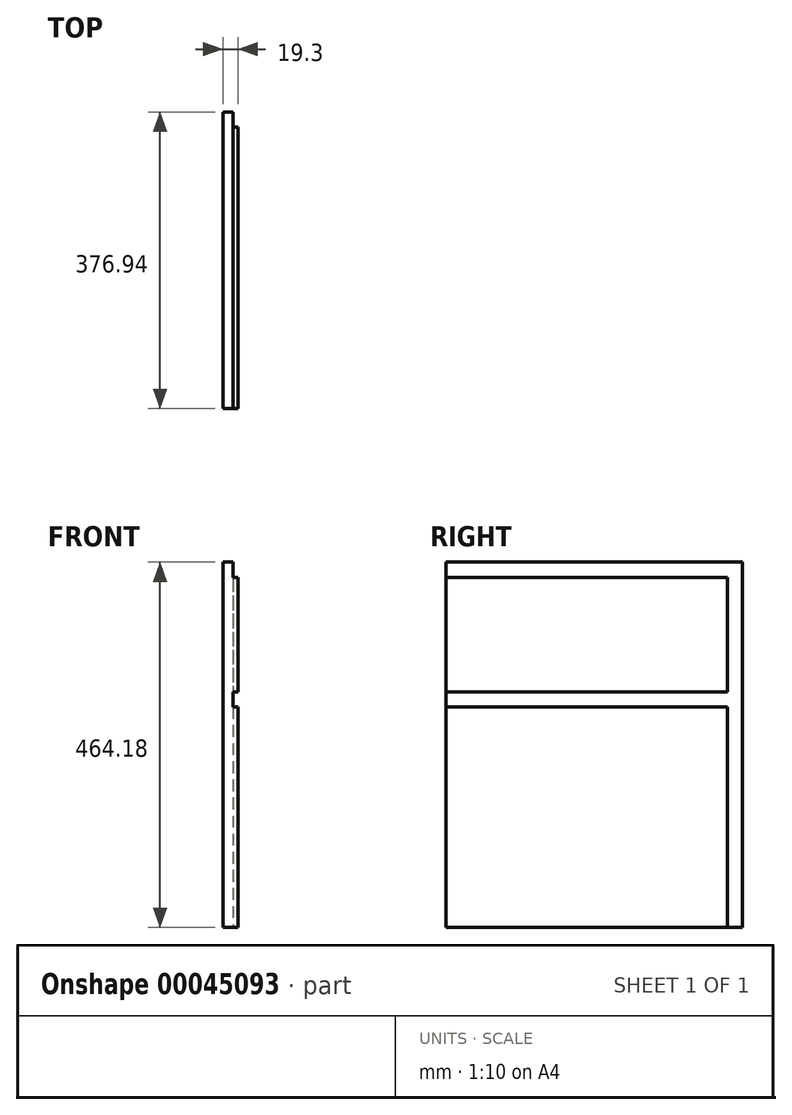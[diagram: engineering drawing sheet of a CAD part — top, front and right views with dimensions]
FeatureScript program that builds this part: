
annotation { "Feature Type Name" : "Feature", "Feature Type Description" : "" }
export const myFeature = defineFeature(function(context is Context, id is Id, definition is map)
    precondition{}
    {
        {
            var Q0;
            Q0=qCreatedBy(makeId("Right.planeOp"),FACE);
            var sketch = newSketch(context, id + "F0", { "sketchPlane" : qUnion([Q0])});
            skLineSegment(sketch, "E0.rect.bottom", {"start": v(-188.47, 232.1) * mm, "end": v(188.47, 232.1) * mm});
            skLineSegment(sketch, "E0.rect.top", {"start": v(-188.47, -232.1) * mm, "end": v(188.47, -232.1) * mm});
            skLineSegment(sketch, "E0.rect.left", {"start": v(-188.47, 232.1) * mm, "end": v(-188.47, -232.1) * mm});
            skLineSegment(sketch, "E0.rect.right", {"start": v(188.47, 232.1) * mm, "end": v(188.47, -232.1) * mm});
            skPoint(sketch, "E0.rect.middle", {"position": v(0, 0) * mm});
            skSolve(sketch);
        }
        {
            var Q0;
            Q0 = qSketchRegion(id + "F0", true);
            extrude(context, id + "F1", {"entities" : qUnion([Q0]), "depth" : 19.3 * mm});
        }
        {
            var Q0;
            Q0=makeQuery(id+"F1.opExtrude","CAP_FACE",FACE,{"disambiguationData":[OSD([sQuery(id+"F0.wireOp",EDGE,"E0.rect.bottom"),sQuery(id+"F0.wireOp",EDGE,"E0.rect.top"),sQuery(id+"F0.wireOp",EDGE,"E0.rect.left"),sQuery(id+"F0.wireOp",EDGE,"E0.rect.right")])],"isStart":false});
            var sketch = newSketch(context, id + "F2", { "sketchPlane" : qUnion([Q0])});
            skLineSegment(sketch, "E1.bottom", {"start": v(-188.47, 67.37) * mm, "end": v(188.47, 67.37) * mm});
            skLineSegment(sketch, "E1.top", {"start": v(-188.47, 48.07) * mm, "end": v(188.47, 48.07) * mm});
            skLineSegment(sketch, "E1.left", {"start": v(-188.47, 67.37) * mm, "end": v(-188.47, 48.07) * mm});
            skLineSegment(sketch, "E1.right", {"start": v(188.47, 67.37) * mm, "end": v(188.47, 48.07) * mm});
            skLineSegment(sketch, "E2.bottom", {"start": v(188.47, 232.1) * mm, "end": v(169.16, 232.1) * mm});
            skLineSegment(sketch, "E2.top", {"start": v(188.47, -232.1) * mm, "end": v(169.16, -232.1) * mm});
            skLineSegment(sketch, "E2.left", {"start": v(188.47, 232.1) * mm, "end": v(188.47, -232.1) * mm});
            skLineSegment(sketch, "E2.right", {"start": v(169.16, 232.1) * mm, "end": v(169.16, -232.1) * mm});
            skLineSegment(sketch, "E3.bottom", {"start": v(-188.47, 232.1) * mm, "end": v(188.47, 232.1) * mm});
            skLineSegment(sketch, "E3.top", {"start": v(-188.47, 212.79) * mm, "end": v(188.47, 212.79) * mm});
            skLineSegment(sketch, "E3.left", {"start": v(-188.47, 232.1) * mm, "end": v(-188.47, 212.79) * mm});
            skLineSegment(sketch, "E3.right", {"start": v(188.47, 232.1) * mm, "end": v(188.47, 212.79) * mm});
            skSolve(sketch);
        }
        {
            var Q0;
            Q0 = qSketchRegion(id + "F2", true);
            extrude(context, id + "F3", {"entities" : qUnion([Q0]), "operationType" : NewBodyOperationType.REMOVE, "oppositeDirection" : true, "depth" : 6.35 * mm});
        }
    });
